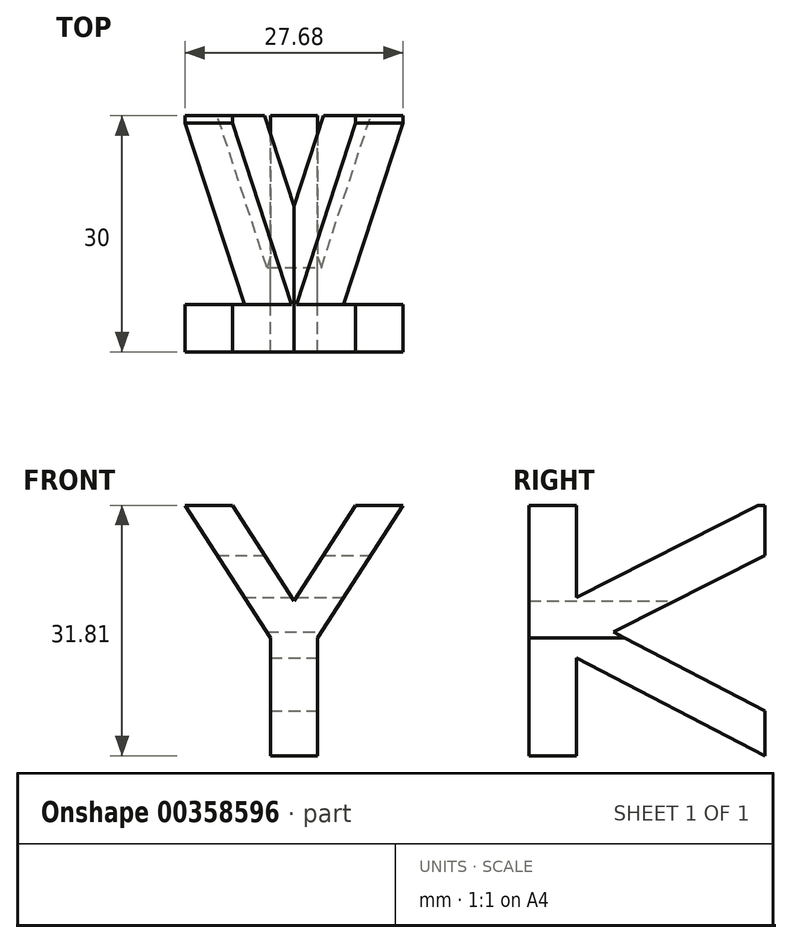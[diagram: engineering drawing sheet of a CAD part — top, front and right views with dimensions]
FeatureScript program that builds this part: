
annotation { "Feature Type Name" : "Feature", "Feature Type Description" : "" }
export const myFeature = defineFeature(function(context is Context, id is Id, definition is map)
    precondition{}
    {
        {
            var Q0;
            Q0=qCreatedBy(makeId("Front.planeOp"),FACE);
            var sketch = newSketch(context, id + "F0", { "sketchPlane" : qUnion([Q0])});
            skLineSegment(sketch, "E0", {"start": v(0, 0) * mm, "end": v(3, 0) * mm});
            skLineSegment(sketch, "E1", {"start": v(3, 0) * mm, "end": v(3, 15) * mm});
            skLineSegment(sketch, "E2", {"start": v(3, 15) * mm, "end": v(13.84, 31.8) * mm});
            skLineSegment(sketch, "E3", {"start": v(13.84, 31.8) * mm, "end": v(7.84, 31.8) * mm});
            skLineSegment(sketch, "E4", {"start": v(7.84, 31.8) * mm, "end": v(0, 19.65) * mm});
            skLineSegment(sketch, "E5.MirrorCS", {"start": v(-7.84, 31.8) * mm, "end": v(0, 19.65) * mm});
            skLineSegment(sketch, "E6.MirrorCS", {"start": v(-13.84, 31.8) * mm, "end": v(-7.84, 31.8) * mm});
            skLineSegment(sketch, "E7.MirrorCS", {"start": v(-3, 15) * mm, "end": v(-13.84, 31.8) * mm});
            skLineSegment(sketch, "E8.MirrorCS", {"start": v(-3, 0) * mm, "end": v(-3, 15) * mm});
            skLineSegment(sketch, "E9.MirrorCS", {"start": v(0, 0) * mm, "end": v(-3, 0) * mm});
            skSolve(sketch);
        }
        {
            var Q0;
            Q0=makeQuery(id+"F0.imprint","IMPRINT",FACE,{"disambiguationData":[TD([[makeQuery(id+"F0.imprint","IMPRINT",EDGE,{"derivedFrom":sQuery(id+"F0.wireOp",EDGE,"E0")}),1.0]])]});
            extrude(context, id + "F1", {"entities" : qUnion([Q0]), "depth" : 30 * mm});
        }
        {
            var Q0;
            Q0=qCreatedBy(makeId("Right.planeOp"),FACE);
            var sketch = newSketch(context, id + "F2", { "sketchPlane" : qUnion([Q0])});
            skLineSegment(sketch, "E10", {"start": v(0, 0) * mm, "end": v(-23.98, 12.43) * mm});
            skLineSegment(sketch, "E11", {"start": v(-23.98, 12.43) * mm, "end": v(-23.98, 0) * mm});
            skLineSegment(sketch, "E12", {"start": v(-23.98, 0) * mm, "end": v(0, 0) * mm});
            skLineSegment(sketch, "E13", {"start": v(0, 32.27) * mm, "end": v(-23.98, 32.27) * mm});
            skLineSegment(sketch, "E14", {"start": v(-23.98, 32.27) * mm, "end": v(-23.98, 20.13) * mm});
            skLineSegment(sketch, "E15", {"start": v(-23.98, 20.13) * mm, "end": v(0, 32.27) * mm});
            skLineSegment(sketch, "E16", {"start": v(0, 25.46) * mm, "end": v(-19.26, 15.71) * mm});
            skLineSegment(sketch, "E17", {"start": v(-19.26, 15.71) * mm, "end": v(0, 5.73) * mm});
            skLineSegment(sketch, "E18", {"start": v(0, 5.73) * mm, "end": v(0, 25.46) * mm});
            skSolve(sketch);
        }
        {
            var Q0;
            Q0 = qSketchRegion(id + "F2", true);
            extrude(context, id + "F3", {"entities" : qUnion([Q0]), "operationType" : NewBodyOperationType.REMOVE, "endBound" : BoundingType.SYMMETRIC, "oppositeDirection" : true, "depth" : 100 * mm});
        }
    });
